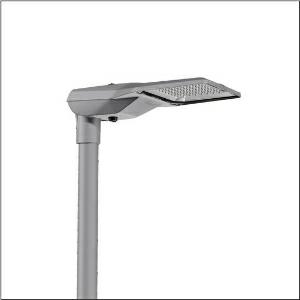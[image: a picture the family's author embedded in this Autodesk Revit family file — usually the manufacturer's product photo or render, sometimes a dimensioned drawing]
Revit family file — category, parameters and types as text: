
# Revit family: streetlight_sl_21_midi___p0_5a_5xe3v33t08lb_b8c4
name_source: partatom
category: Lighting Fixtures
units: mm (PartAtom-declared; Revit-internal decimal feet)

## family parameters
Cut with Voids When Loaded = No
Host = Face
Light Source = No
Part Type = Normal
Room Calculation Point = No
Round Connector Dimension = Use Diameter
Shared = No

## types (1)
- --- (1 x LED, 14100 lm, 99.6 W, 3000K)
    Apparent Load = 100 VA
    CIE Flux Codes = 37 73 96 100 100
    Color Rendering = 70
    Color Temperature = 3000K
    Default Elevation = 1800 mm
    Description = Streetlight SL 21 midi, mast luminaire, primary light control with lens, of PMMA, primary optical cover: cover, of toughened safety glass, transparent, light distribution: P0.5a, light emission: direct distribution, primary light characteristic: asymmetric, installation type: post-top, side-entry, LED, High Power LED, rated luminous flux: 14.100lm, luminous efficacy: 142lm/W, light colour: 730, colour temperature: 3000K, control gear: D4i, control: pre-setting: logarithmic dimming characteristic, flexible luminous flux parameterisation, time-dependent luminous flux control, constant luminous flux control, overheat protection, mains connection: 230..240V, AC, 50/60Hz, start of lifetime: 100W, end of service life: 102W, reduction: 46W, luminaire housing, of diecast aluminium, powder-coated, Siteco® metallic grey (DB 702S), corrosivity category C5 mid according to DIN EN ISO 12944, multi-level sealing system, sealing non-destructively replaceable, inclination adjustable: 0°, 5°, 10°, 15°, please order mast flange separately, length: 644mm, width: 335mm, height: 110mm, mast flange for spigot size: 42mm (side-entry): 5XC10008XM4, 60/48mm (side-entry/post-top): 5XC10108XM2, 76/60mm (side-entry/post-top): 5XC10108XM1, mounting height: 4..8m, Smart Interface below and above, protection rating (complete): IP66, insulation class (complete): insulation class II (safety insulation), certification: CE, ENEC, ENEC+, VDE, impact resistance: IK10, permissible operating ambient temperature for outdoor applications: -40..+50°C, standard-compliant lighting for roads and squares, packaging unit: 1 piece

Light Distribution: P0.5a
    Height = 111 mm
    Lamp = 1 x LED
    Lamp Light Flux = 14100 lm
    Lamp Power = 99.6 W
    Lamp count = 1
    Length = 644 mm
    Luminous efficacy = 142 lm/W
    Manufacturer = Siteco
    ModVariant = No
    Model = 5XE3V33T08LB
    Number of Poles = 1
    OnlyDefault = Yes
    Power Factor = 1
    Product Name = Streetlight SL 21 midi | P0.5a
    Product group = mast luminaire | pylon top
    ProductGroupID = 6100
    Protection Class = Protection class II
    Protection Degree = IP 66
    RLX_Detail_Level = 1
    RLX_Emergency_Light_Flux = 0 lm
    RLX_Emergency_Type = 0
    RLX_Emergency_Type_DB = No
    RlxData = <blob elided: 26465 chars, md5=ba9f4702>
    Socket = socket
    Standby Power = 0 W
    System Light Flux = 14100 lm
    System Power = 100 W
    Type Comments = factory setting: luminous flux: 100 % | dim-lin: 254 | 1020 mA
    Type Image = l_1004304.jpg
    URL = http://relux.com
    VarID = @adj_013053
    Voltage = 0 V
    Weight = 0.00 kg
    Width = 336 mm

## geometry (parser evidence)
native form markers: Blend x4, Sweep x10
no freeform markers — native parametric forms only
